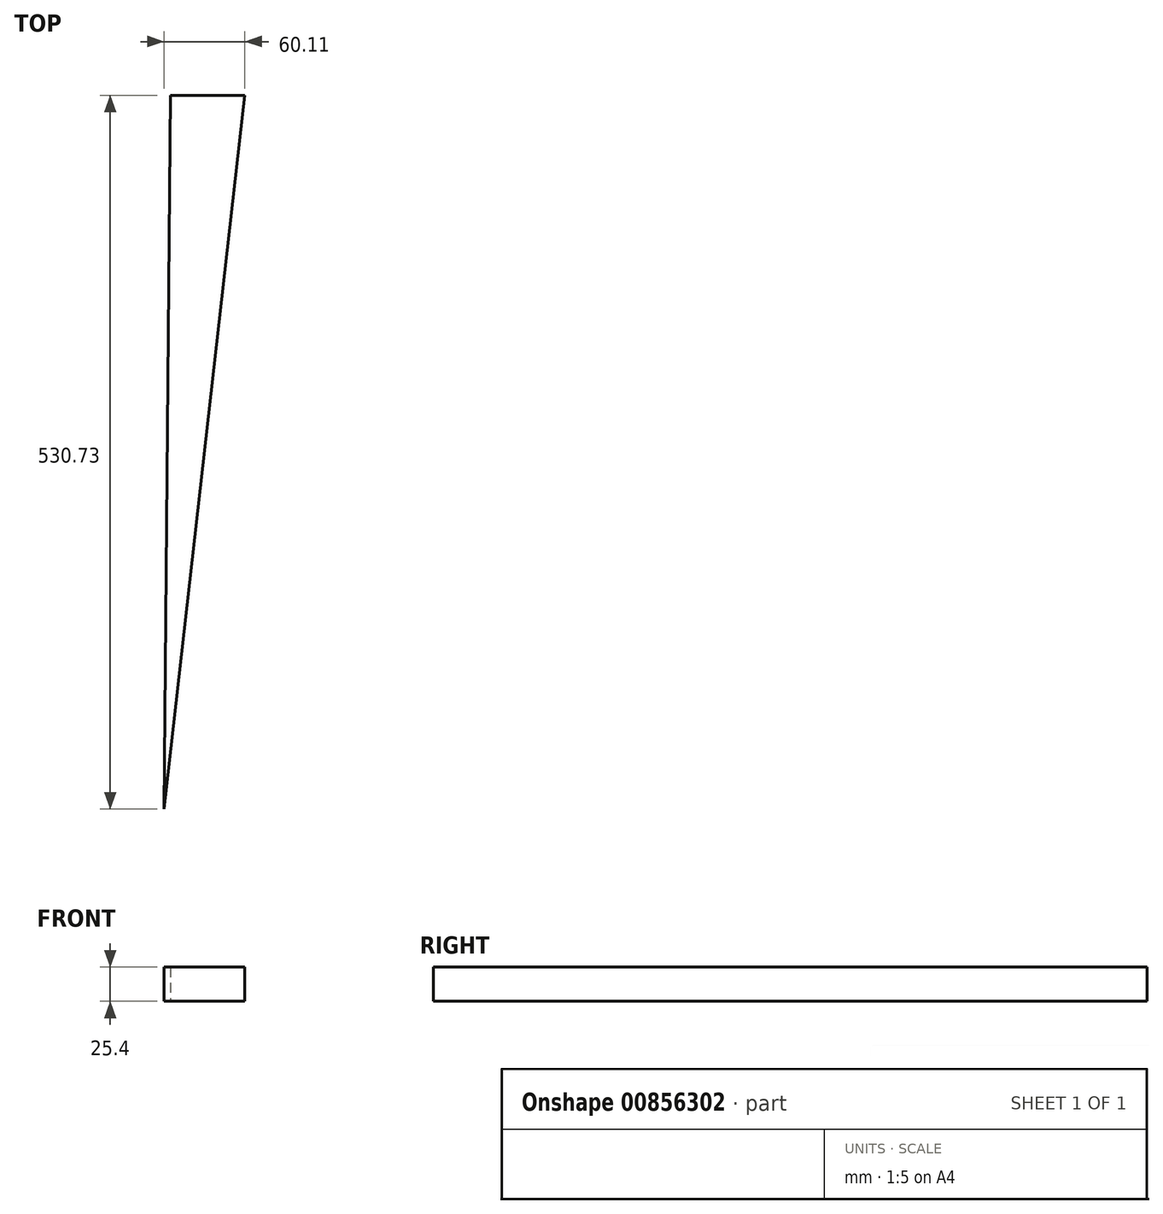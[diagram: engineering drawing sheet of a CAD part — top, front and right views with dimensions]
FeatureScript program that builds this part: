
annotation { "Feature Type Name" : "Feature", "Feature Type Description" : "" }
export const myFeature = defineFeature(function(context is Context, id is Id, definition is map)
    precondition{}
    {
        {
            var Q0;
            Q0=qCreatedBy(makeId("Top.planeOp"),FACE);
            var sketch = newSketch(context, id + "F0", { "sketchPlane" : qUnion([Q0])});
            skLineSegment(sketch, "E0", {"start": v(-27.24, 749.72) * mm, "end": v(28.27, 749.72) * mm});
            skLineSegment(sketch, "E1", {"start": v(28.27, 749.72) * mm, "end": v(-31.84, 218.99) * mm});
            skLineSegment(sketch, "E2", {"start": v(-31.84, 218.99) * mm, "end": v(-27.24, 749.72) * mm});
            skSolve(sketch);
        }
        {
            var Q0;
            Q0=makeQuery(id+"F0.imprint","IMPRINT",FACE,{"disambiguationData":[TD([[makeQuery(id+"F0.imprint","IMPRINT",EDGE,{"derivedFrom":sQuery(id+"F0.wireOp",EDGE,"E0")}),-1.0]])]});
            extrude(context, id + "F1", {"entities" : qUnion([Q0]), "depth" : 25.4 * mm, "offsetDistance" : 25.4 * mm});
        }
    });
